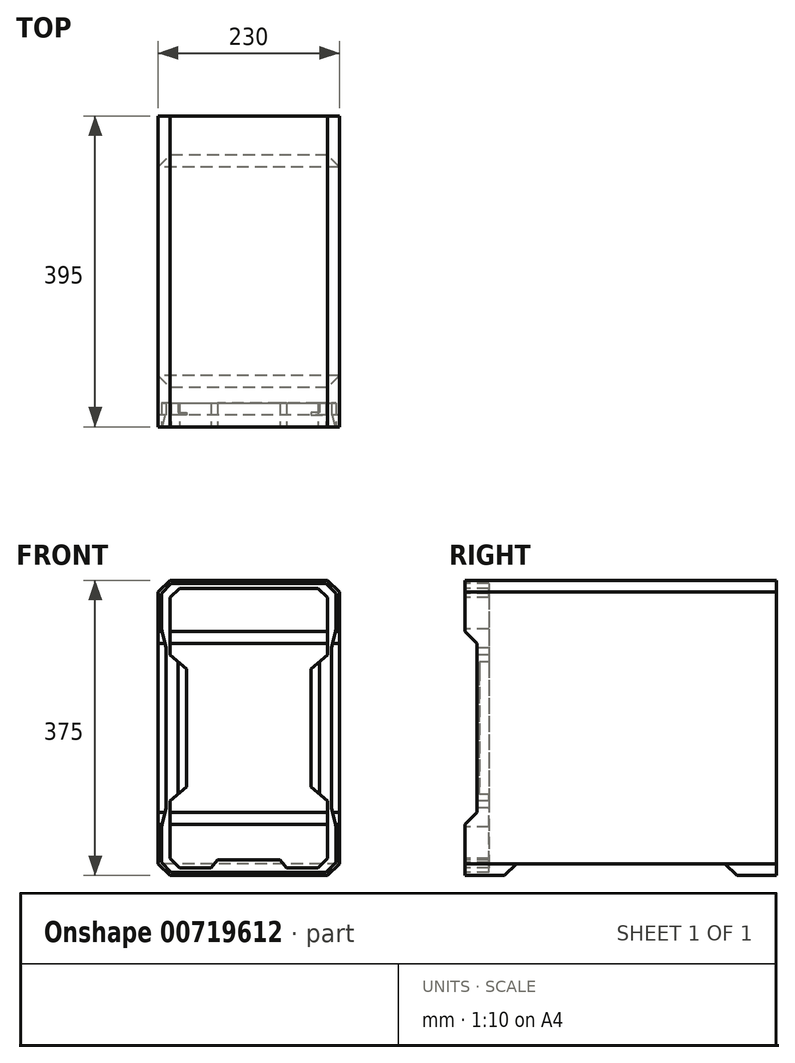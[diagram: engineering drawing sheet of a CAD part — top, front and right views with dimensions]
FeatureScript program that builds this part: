
annotation { "Feature Type Name" : "Feature", "Feature Type Description" : "" }
export const myFeature = defineFeature(function(context is Context, id is Id, definition is map)
    precondition{}
    {
        {
            var Q0;
            Q0=qCreatedBy(makeId("Front.planeOp"),FACE);
            var sketch = newSketch(context, id + "F0", { "sketchPlane" : qUnion([Q0])});
            skLineSegment(sketch, "E0.bottom", {"start": v(0, 0) * mm, "end": v(230, 0) * mm});
            skLineSegment(sketch, "E0.top", {"start": v(0, 375) * mm, "end": v(230, 375) * mm});
            skLineSegment(sketch, "E0.left", {"start": v(0, 0) * mm, "end": v(0, 375) * mm});
            skLineSegment(sketch, "E0.right", {"start": v(230, 0) * mm, "end": v(230, 375) * mm});
            skSolve(sketch);
        }
        {
            var Q0;
            Q0 = qSketchRegion(id + "F0", true);
            extrude(context, id + "F1", {"entities" : qUnion([Q0]), "oppositeDirection" : true, "depth" : 395 * mm, "offsetDistance" : 25 * mm});
        }
        {
            var Q0;
            Q0=makeQuery(id+"F1.opExtrude","SWEPT_EDGE",EDGE,{"disambiguationData":[OSD([sQuery(id+"F0.wireOp",EDGE,"E0.top"),sQuery(id+"F0.wireOp",EDGE,"E0.left")])]});
            var Q1;
            Q1=makeQuery(id+"F1.opExtrude","SWEPT_EDGE",EDGE,{"disambiguationData":[OSD([sQuery(id+"F0.wireOp",EDGE,"E0.bottom"),sQuery(id+"F0.wireOp",EDGE,"E0.left")])]});
            var Q2;
            Q2=makeQuery(id+"F1.opExtrude","SWEPT_EDGE",EDGE,{"disambiguationData":[OSD([sQuery(id+"F0.wireOp",EDGE,"E0.top"),sQuery(id+"F0.wireOp",EDGE,"E0.right")])]});
            var Q3;
            Q3=makeQuery(id+"F1.opExtrude","SWEPT_EDGE",EDGE,{"disambiguationData":[OSD([sQuery(id+"F0.wireOp",EDGE,"E0.bottom"),sQuery(id+"F0.wireOp",EDGE,"E0.right")])]});
            chamfer(context, id + "F2", {"entities" : qUnion([Q0, Q1, Q2, Q3]), "width" : 15 * mm, "tangentPropagation" : true});
        }
        {
            var Q0;
            Q0=makeQuery(id+"F1.opExtrude","SWEPT_FACE",FACE,{"disambiguationData":[OSD([sQuery(id+"F0.wireOp",EDGE,"E0.left")])]});
            var sketch = newSketch(context, id + "F3", { "sketchPlane" : qUnion([Q0])});
            skLineSegment(sketch, "E1", {"start": v(-65, 15) * mm, "end": v(-330, 15) * mm});
            skLineSegment(sketch, "E2", {"start": v(-330, 15) * mm, "end": v(-345, 0) * mm});
            skLineSegment(sketch, "E3", {"start": v(-395, 187.5) * mm, "end": v(0, 187.5) * mm, "construction": true});
            skLineSegment(sketch, "E4", {"start": v(-15, 295) * mm, "end": v(0, 310) * mm});
            skLineSegment(sketch, "E5.MirrorCS", {"start": v(-15, 80) * mm, "end": v(0, 65) * mm});
            skLineSegment(sketch, "E6", {"start": v(-15, 295) * mm, "end": v(-15, 80) * mm});
            skLineSegment(sketch, "E7", {"start": v(-345, 0) * mm, "end": v(-50, 0) * mm});
            skLineSegment(sketch, "E8", {"start": v(-197.5, 187.5) * mm, "end": v(-197.5, 106.14) * mm, "construction": true});
            skLineSegment(sketch, "E9.MirrorCS", {"start": v(-65, 15) * mm, "end": v(-50, 0) * mm});
            skSolve(sketch);
        }
        {
            var Q0;
            {var subQ0=sQuery(id+"F3.wireOp",EDGE,"E4");Q0=makeQuery(id+"F3.imprint","IMPRINT",FACE,{"disambiguationData":[TD([[makeQuery(id+"F3.imprint","IMPRINT",EDGE,{"derivedFrom":subQ0}),-1.0]])]});}
            var Q1;
            Q1=makeQuery(id+"F3.imprint","IMPRINT",FACE,{"disambiguationData":[TD([[makeQuery(id+"F3.imprint","IMPRINT",EDGE,{"derivedFrom":sQuery(id+"F3.wireOp",EDGE,"E1")}),-1.0]])]});
            extrude(context, id + "F4", {"entities" : qUnion([Q0, Q1]), "operationType" : NewBodyOperationType.REMOVE, "endBound" : BoundingType.THROUGH_ALL, "oppositeDirection" : true, "depth" : 25 * mm, "offsetDistance" : 25 * mm});
        }
        {
            var Q0;
            {var subQ0=sQuery(id+"F0.wireOp",EDGE,"E0.right");var subQ1=sQuery(id+"F0.wireOp",EDGE,"E0.left");var subQ2=sQuery(id+"F0.wireOp",EDGE,"E0.top");Q0=makeQuery(id+"F4.boolean.opBoolean","SPLIT",FACE,{"disambiguationData":[TD([makeQuery(id+"F1.opExtrude","SWEPT_FACE",FACE,{"disambiguationData":[OSD([subQ2])]})])],"derivedFrom":makeQuery(id+"F1.opExtrude","CAP_FACE",FACE,{"disambiguationData":[OSD([sQuery(id+"F0.wireOp",EDGE,"E0.bottom"),subQ2,subQ1,subQ0])],"isStart":true})});}
            var sketch = newSketch(context, id + "F5", { "sketchPlane" : qUnion([Q0])});
            skLineSegment(sketch, "E10", {"start": v(115, 375) * mm, "end": v(115, 0) * mm, "construction": true});
            skLineSegment(sketch, "E11", {"start": v(15, 353) * mm, "end": v(15, 280) * mm});
            skLineSegment(sketch, "E12", {"start": v(15, 280) * mm, "end": v(25, 271.6) * mm});
            skLineSegment(sketch, "E13", {"start": v(25, 271.6) * mm, "end": v(25, 103.4) * mm});
            skLineSegment(sketch, "E14", {"start": v(15, 95) * mm, "end": v(15, 22) * mm});
            skLineSegment(sketch, "E15", {"start": v(67, 10) * mm, "end": v(75.4, 20) * mm});
            skLineSegment(sketch, "E16", {"start": v(75.4, 20) * mm, "end": v(115, 20) * mm});
            skLineSegment(sketch, "E17", {"start": v(15, 353) * mm, "end": v(27, 365) * mm});
            skLineSegment(sketch, "E18", {"start": v(27, 365) * mm, "end": v(115, 365) * mm});
            skLineSegment(sketch, "E19", {"start": v(115, 187.5) * mm, "end": v(25, 187.5) * mm, "construction": true});
            skLineSegment(sketch, "E20.MirrorCS", {"start": v(15, 95) * mm, "end": v(25, 103.4) * mm});
            skLineSegment(sketch, "E21.MirrorCS", {"start": v(15, 22) * mm, "end": v(27, 10) * mm});
            skLineSegment(sketch, "E22", {"start": v(27, 10) * mm, "end": v(67, 10) * mm});
            skLineSegment(sketch, "E23.MirrorCS", {"start": v(203, 365) * mm, "end": v(115, 365) * mm});
            skLineSegment(sketch, "E24.MirrorCS", {"start": v(215, 353) * mm, "end": v(203, 365) * mm});
            skLineSegment(sketch, "E25.MirrorCS", {"start": v(215, 353) * mm, "end": v(215, 280) * mm});
            skLineSegment(sketch, "E26.MirrorCS", {"start": v(215, 280) * mm, "end": v(205, 271.6) * mm});
            skLineSegment(sketch, "E27.MirrorCS", {"start": v(205, 271.6) * mm, "end": v(205, 103.4) * mm});
            skLineSegment(sketch, "E28.MirrorCS", {"start": v(215, 95) * mm, "end": v(215, 22) * mm});
            skLineSegment(sketch, "E29.MirrorCS", {"start": v(215, 95) * mm, "end": v(205, 103.4) * mm});
            skLineSegment(sketch, "E30.MirrorCS", {"start": v(215, 22) * mm, "end": v(203, 10) * mm});
            skLineSegment(sketch, "E31.MirrorCS", {"start": v(203, 10) * mm, "end": v(163, 10) * mm});
            skLineSegment(sketch, "E32.MirrorCS", {"start": v(163, 10) * mm, "end": v(154.6, 20) * mm});
            skLineSegment(sketch, "E33.MirrorCS", {"start": v(154.6, 20) * mm, "end": v(115, 20) * mm});
            skLineSegment(sketch, "E34.0", {"start": v(16.66, 371) * mm, "end": v(4, 358.34) * mm});
            skLineSegment(sketch, "E35", {"start": v(4, 358.34) * mm, "end": v(4, 313.34) * mm});
            skLineSegment(sketch, "E36", {"start": v(4, 313.34) * mm, "end": v(10, 289.34) * mm});
            skLineSegment(sketch, "E37.MirrorCS", {"start": v(16.66, 4) * mm, "end": v(4, 16.66) * mm});
            skLineSegment(sketch, "E38.MirrorCS", {"start": v(4, 16.66) * mm, "end": v(4, 61.66) * mm});
            skLineSegment(sketch, "E39.MirrorCS", {"start": v(4, 61.66) * mm, "end": v(10, 85.66) * mm});
            skLineSegment(sketch, "E40", {"start": v(16.66, 371) * mm, "end": v(115, 371) * mm});
            skLineSegment(sketch, "E41", {"start": v(16.66, 4) * mm, "end": v(115, 4) * mm});
            skLineSegment(sketch, "E42", {"start": v(10, 289.34) * mm, "end": v(10, 85.66) * mm});
            skLineSegment(sketch, "E43.MirrorCS", {"start": v(213.34, 371) * mm, "end": v(115, 371) * mm});
            skLineSegment(sketch, "E44.MirrorCS", {"start": v(213.34, 371) * mm, "end": v(226, 358.34) * mm});
            skLineSegment(sketch, "E45.MirrorCS", {"start": v(226, 358.34) * mm, "end": v(226, 313.34) * mm});
            skLineSegment(sketch, "E46.MirrorCS", {"start": v(226, 313.34) * mm, "end": v(220, 289.34) * mm});
            skLineSegment(sketch, "E47.MirrorCS", {"start": v(220, 289.34) * mm, "end": v(220, 85.66) * mm});
            skLineSegment(sketch, "E48.MirrorCS", {"start": v(226, 61.66) * mm, "end": v(220, 85.66) * mm});
            skLineSegment(sketch, "E49.MirrorCS", {"start": v(226, 16.66) * mm, "end": v(226, 61.66) * mm});
            skLineSegment(sketch, "E50.MirrorCS", {"start": v(213.34, 4) * mm, "end": v(226, 16.66) * mm});
            skLineSegment(sketch, "E51.MirrorCS", {"start": v(213.34, 4) * mm, "end": v(115, 4) * mm});
            skSolve(sketch);
        }
        {
            var Q0;
            {var subQ9=sQuery(id+"F5.wireOp",EDGE,"E12");Q0=makeQuery(id+"F5.imprint","IMPRINT",FACE,{"disambiguationData":[TD([[makeQuery(id+"F5.imprint","IMPRINT",EDGE,{"derivedFrom":subQ9}),-1.0]])]});}
            var Q1;
            {var subQ10=sQuery(id+"F5.wireOp",EDGE,"E17");Q1=makeQuery(id+"F5.imprint","IMPRINT",FACE,{"disambiguationData":[TD([[makeQuery(id+"F5.imprint","IMPRINT",EDGE,{"derivedFrom":subQ10}),1.0]])]});}
            extrude(context, id + "F6", {"entities" : qUnion([Q0, Q1]), "operationType" : NewBodyOperationType.REMOVE, "oppositeDirection" : true, "depth" : 30 * mm, "offsetDistance" : 25 * mm});
        }
        {
            var Q0;
            Q0=makeQuery(id+"F6.boolean.opBoolean","SPLIT",FACE,{"disambiguationData":[TD([makeQuery(id+"F6.opExtrude","SWEPT_FACE",FACE,{"disambiguationData":[OSD([sQuery(id+"F5.wireOp",EDGE,"E11")])]})])],"derivedFrom":makeQuery(id+"F4.boolean.opBoolean","COPY",FACE,{"derivedFrom":makeQuery(id+"F4.opExtrude","SWEPT_FACE",FACE,{"disambiguationData":[OSD([sQuery(id+"F3.wireOp",EDGE,"E6")])]})})});
            var sketch = newSketch(context, id + "F7", { "sketchPlane" : qUnion([Q0])});
            skLineSegment(sketch, "E52", {"start": v(25, 271.6) * mm, "end": v(36, 262.38) * mm});
            skLineSegment(sketch, "E53", {"start": v(25, 103.4) * mm, "end": v(36, 112.62) * mm});
            skLineSegment(sketch, "E54", {"start": v(115, 295) * mm, "end": v(115, 80) * mm, "construction": true});
            skLineSegment(sketch, "E55", {"start": v(36, 262.38) * mm, "end": v(36, 112.62) * mm});
            skLineSegment(sketch, "E56.MirrorCS", {"start": v(205, 271.6) * mm, "end": v(194, 262.38) * mm});
            skLineSegment(sketch, "E57.MirrorCS", {"start": v(194, 262.38) * mm, "end": v(194, 112.62) * mm});
            skLineSegment(sketch, "E58.MirrorCS", {"start": v(205, 103.4) * mm, "end": v(194, 112.62) * mm});
            skSolve(sketch);
        }
        {
            var Q0;
            Q0=makeQuery(id+"F7.imprint","IMPRINT",FACE,{"disambiguationData":[TD([[makeQuery(id+"F7.imprint","IMPRINT",EDGE,{"derivedFrom":sQuery(id+"F7.wireOp",EDGE,"E52")}),-1.0]])]});
            var Q1;
            Q1=makeQuery(id+"F7.imprint","IMPRINT",FACE,{"disambiguationData":[TD([[makeQuery(id+"F7.imprint","IMPRINT",EDGE,{"derivedFrom":sQuery(id+"F7.wireOp",EDGE,"E56.MirrorCS")}),1.0]])]});
            extrude(context, id + "F8", {"entities" : qUnion([Q0, Q1]), "operationType" : NewBodyOperationType.REMOVE, "oppositeDirection" : true, "depth" : 3 * mm, "offsetDistance" : 25 * mm});
        }
    });
